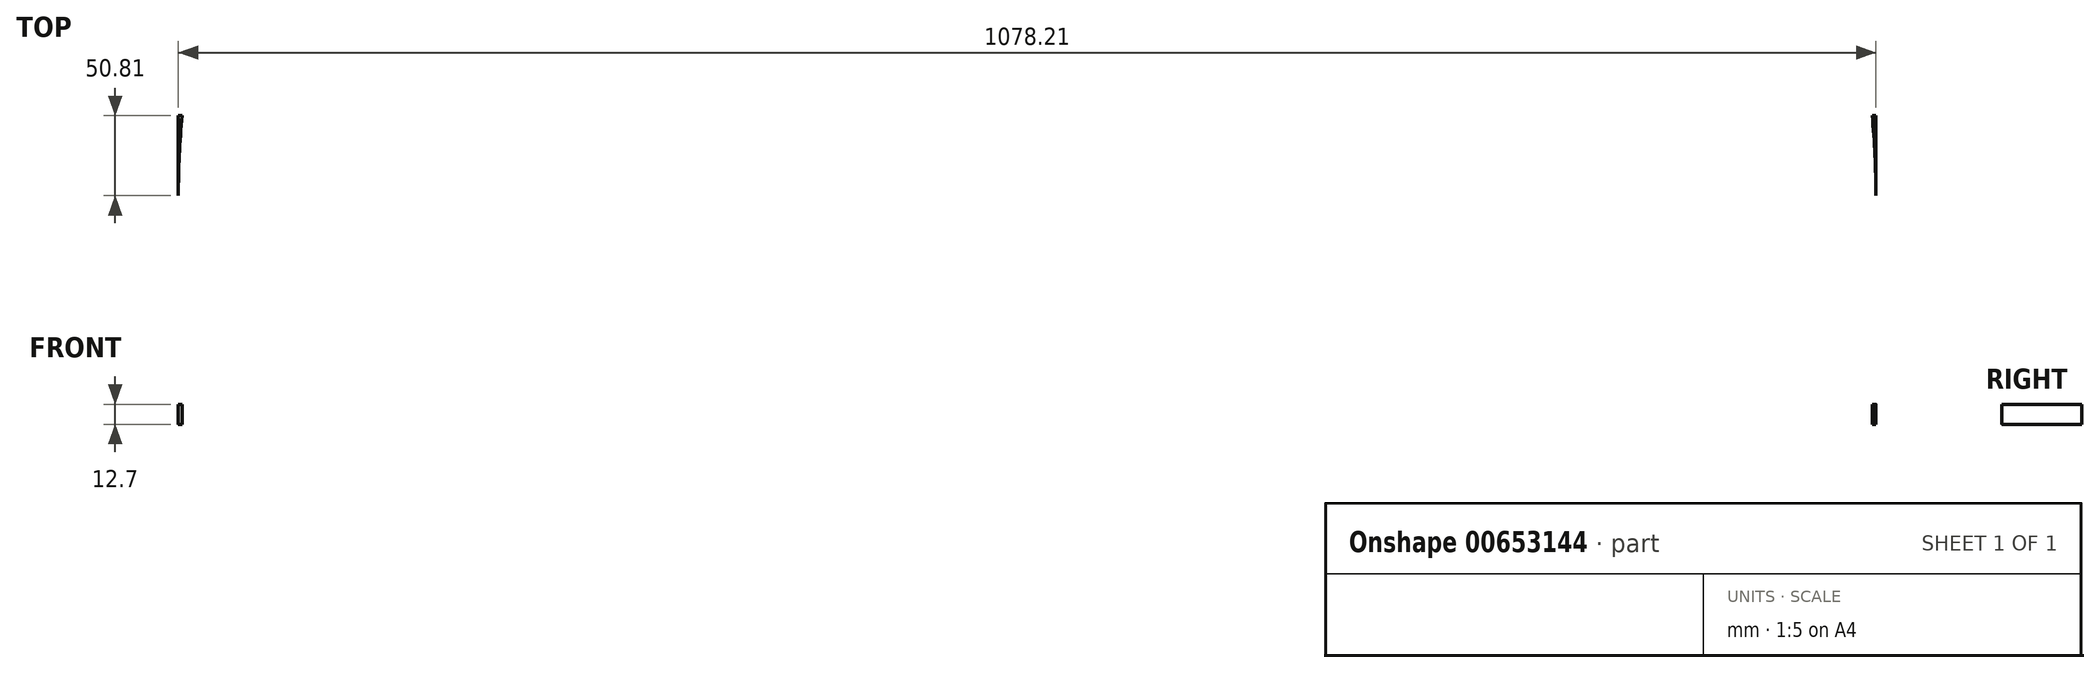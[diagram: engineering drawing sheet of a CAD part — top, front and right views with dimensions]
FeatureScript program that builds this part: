
annotation { "Feature Type Name" : "Feature", "Feature Type Description" : "" }
export const myFeature = defineFeature(function(context is Context, id is Id, definition is map)
    precondition{}
    {
        {
            var Q0;
            Q0=qCreatedBy(makeId("Top.planeOp"),FACE);
            var sketch = newSketch(context, id + "F0", { "sketchPlane" : qUnion([Q0])});
            skPoint(sketch, "E0", {"position": v(736.6, 0) * mm});
            skPoint(sketch, "E1", {"position": v(800.1, 0) * mm});
            skPoint(sketch, "E2", {"position": v(838.2, 0) * mm});
            skPoint(sketch, "E3", {"position": v(1168.4, 0) * mm});
            skPoint(sketch, "E4", {"position": v(1219.2, 0) * mm});
            skPoint(sketch, "E5", {"position": v(1270, -0.04) * mm});
            skLineSegment(sketch, "E6.top", {"start": v(736.6, 50.8) * mm, "end": v(800.1, 50.8) * mm});
            skLineSegment(sketch, "E6.left", {"start": v(736.6, 0) * mm, "end": v(736.6, 50.8) * mm});
            skLineSegment(sketch, "E6.right", {"start": v(800.1, 0) * mm, "end": v(800.1, 50.8) * mm});
            skLineSegment(sketch, "E7.top", {"start": v(838.2, 152.4) * mm, "end": v(1168.4, 152.4) * mm});
            skLineSegment(sketch, "E7.left", {"start": v(838.2, 0) * mm, "end": v(838.2, 152.4) * mm});
            skLineSegment(sketch, "E8.top", {"start": v(1219.2, 50.81) * mm, "end": v(1270, 50.81) * mm});
            skLineSegment(sketch, "E8.left", {"start": v(1219.2, 0) * mm, "end": v(1219.2, 50.81) * mm});
            skLineSegment(sketch, "E8.right", {"start": v(1270, 0.01) * mm, "end": v(1270, 50.81) * mm});
            skLineSegment(sketch, "E9", {"start": v(800.1, 0) * mm, "end": v(838.2, 0) * mm});
            skLineSegment(sketch, "E10", {"start": v(1168.4, 0) * mm, "end": v(1219.2, 0) * mm});
            skLineSegment(sketch, "E11", {"start": v(1270, -0.04) * mm, "end": v(1371.6, -0.04) * mm});
            skLineSegment(sketch, "E12", {"start": v(90.2, 0) * mm, "end": v(191.8, 0) * mm});
            skLineSegment(sketch, "E13", {"start": v(191.8, 0) * mm, "end": v(191.8, 50.8) * mm});
            skLineSegment(sketch, "E14", {"start": v(191.8, 50.8) * mm, "end": v(242.6, 50.8) * mm});
            skLineSegment(sketch, "E15", {"start": v(242.6, 50.8) * mm, "end": v(242.6, 0) * mm});
            skLineSegment(sketch, "E16", {"start": v(242.6, 0) * mm, "end": v(736.6, 0) * mm});
            skArc(sketch, "E17", {"start": v(1371.6, -0.04) * mm, "mid": v(730.92, 639.27) * mm, "end": v(90.2, 0) * mm});
            skLineSegment(sketch, "E18", {"start": v(1168.4, 152.4) * mm, "end": v(1168.4, 0) * mm});
            skArc(sketch, "E19", {"start": v(1270, 0.01) * mm, "mid": v(730.9, 539.1) * mm, "end": v(191.8, 0) * mm});
            skSolve(sketch);
        }
        {
            var Q0;
            {var subQ0=sQuery(id+"F0.wireOp",EDGE,"E8.right");Q0=makeQuery(id+"F0.imprint","IMPRINT",FACE,{"disambiguationData":[TD([[makeQuery(id+"F0.imprint","IMPRINT",EDGE,{"derivedFrom":subQ0}),1.0]])]});}
            var Q1;
            {var subQ0=sQuery(id+"F0.wireOp",EDGE,"E13");Q1=makeQuery(id+"F0.imprint","IMPRINT",FACE,{"disambiguationData":[TD([[makeQuery(id+"F0.imprint","IMPRINT",EDGE,{"derivedFrom":subQ0}),-1.0]])]});}
            extrude(context, id + "F1", {"entities" : qUnion([Q0, Q1]), "depth" : 12.7 * mm, "offsetDistance" : 25.4 * mm});
        }
    });
